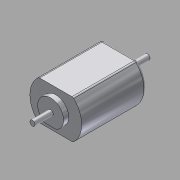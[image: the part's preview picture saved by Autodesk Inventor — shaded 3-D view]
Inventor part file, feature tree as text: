
AUTODESK INVENTOR PART (.ipt)
format: ipt  version: 2015 (Build 190159000, 159)  size: 137,216 bytes
history: native  units: in
note: dims shown in document units (in); Inventor stores cm internally (conversion verified against a paired STEP export)
features: sketch x5, other x3
ambient origin geometry x8: Origin, YZ Plane, XZ Plane, XY Plane, X Axis, Y Axis, Z Axis, Center Point
bodies: Solid1 (feature_tree)
feature tree (8):
  other  "motor.ipt"
  other  "Solid1::motor.ipt"
  other  "TaggingFeature1"
  sketch  "Sketch1"  dims[d0=0.3937in]
  sketch  "Sketch2"
  sketch  "Sketch3"
  sketch  "Sketch4"
  sketch  "Sketch5"
